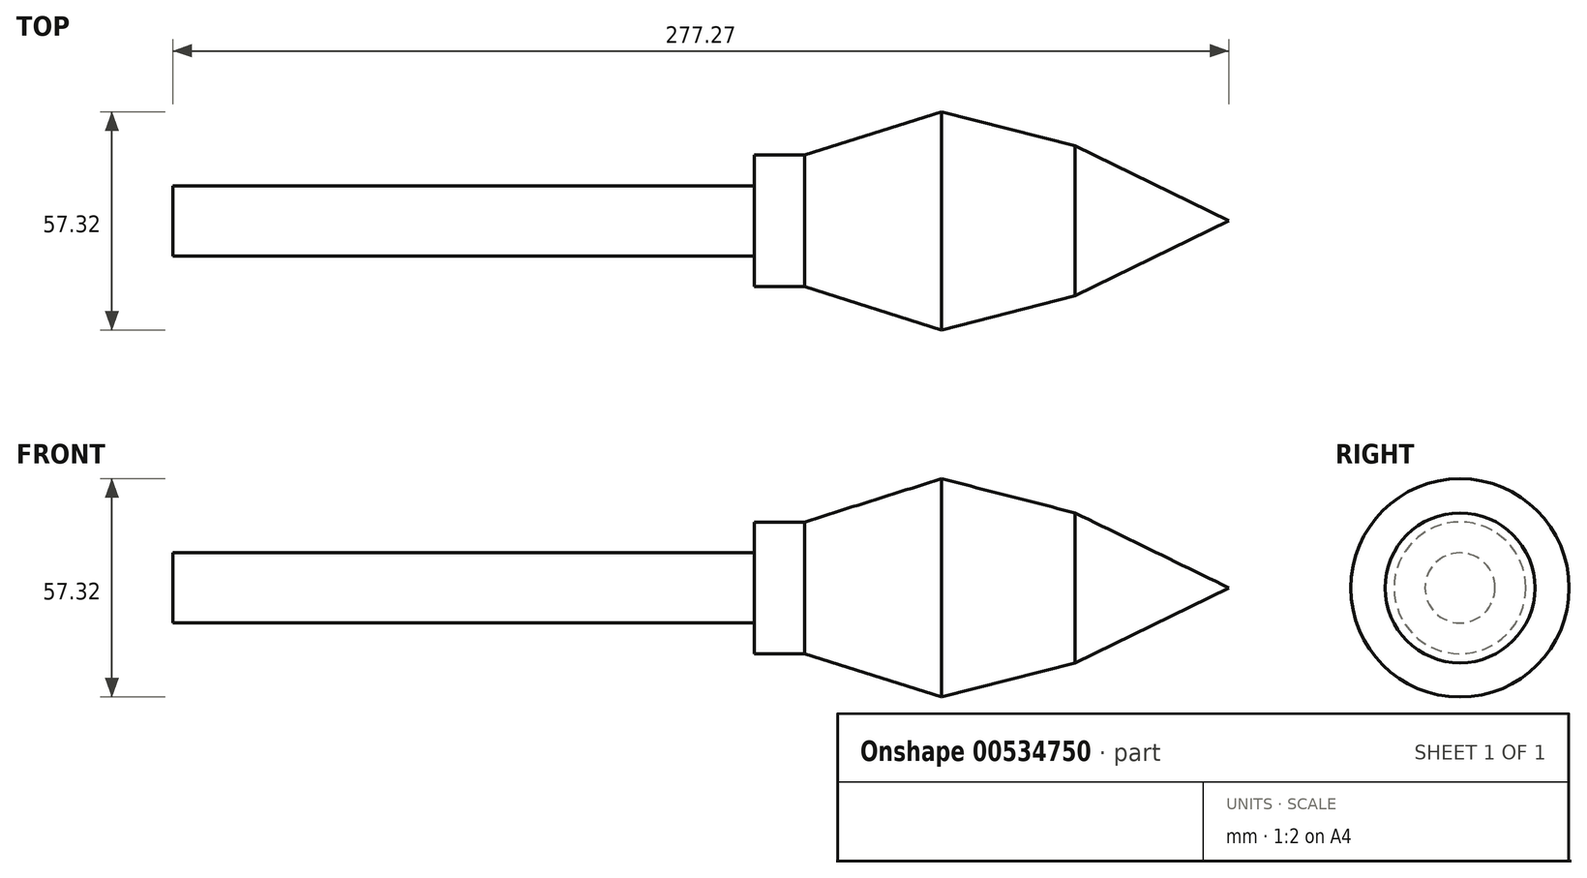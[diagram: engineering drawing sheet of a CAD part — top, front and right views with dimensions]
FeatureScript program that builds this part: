
annotation { "Feature Type Name" : "Feature", "Feature Type Description" : "" }
export const myFeature = defineFeature(function(context is Context, id is Id, definition is map)
    precondition{}
    {
        {
            var Q0;
            Q0=qCreatedBy(makeId("Top.planeOp"),FACE);
            var sketch = newSketch(context, id + "F0", { "sketchPlane" : qUnion([Q0])});
            skLineSegment(sketch, "E0", {"start": v(19.76, 0) * mm, "end": v(19.76, 9.2) * mm});
            skLineSegment(sketch, "E1", {"start": v(19.76, 9.2) * mm, "end": v(19.76, 17.28) * mm});
            skLineSegment(sketch, "E2", {"start": v(19.76, 17.28) * mm, "end": v(32.94, 17.28) * mm});
            skLineSegment(sketch, "E3", {"start": v(32.94, 17.28) * mm, "end": v(68.87, 28.66) * mm});
            skLineSegment(sketch, "E4", {"start": v(68.87, 28.66) * mm, "end": v(103.9, 19.68) * mm});
            skLineSegment(sketch, "E5", {"start": v(103.9, 19.68) * mm, "end": v(144.33, 0) * mm});
            skLineSegment(sketch, "E6", {"start": v(19.76, 0) * mm, "end": v(144.33, 0) * mm});
            skLineSegment(sketch, "E7", {"start": v(19.76, 9.2) * mm, "end": v(-132.94, 9.2) * mm});
            skLineSegment(sketch, "E8", {"start": v(-132.94, 9.2) * mm, "end": v(-132.94, 0) * mm});
            skLineSegment(sketch, "E9", {"start": v(-132.94, 0) * mm, "end": v(19.76, 0) * mm});
            skSolve(sketch);
        }
        {
            var Q0;
            Q0 = qSketchRegion(id + "F0", true);
            var Q1;
            Q1=sQuery(id+"F0.wireOp",EDGE,"E6");
            revolve(context, id + "F1", {"entities" : qUnion([Q0]), "axis" : qUnion([Q1]), "revolveType" : RevolveType.FULL});
        }
    });
